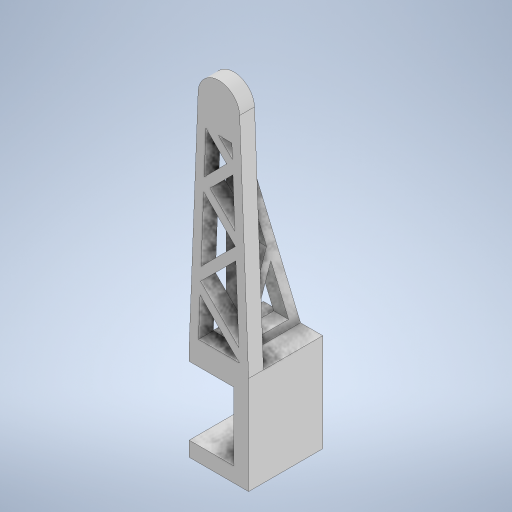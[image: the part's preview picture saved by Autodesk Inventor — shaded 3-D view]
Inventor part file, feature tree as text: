
AUTODESK INVENTOR PART (.ipt)
format: ipt  version: 2023 (Build 270158000, 158)  size: 342,016 bytes
history: native  units: mm
features: extrude x4, sketch x4, other x2
ambient origin geometry x8: Origin, YZ Plane, XZ Plane, XY Plane, X Axis, Y Axis, Z Axis, Center Point
bodies: Body1 (feature_tree)
feature tree (10):
  other  "솔리드1"
  extrude  "돌출1"  Depth=66.0mm
  extrude  "돌출2"  Depth=10.0mm
  other  "작업 평면1"
  extrude  "돌출3"  Depth=10.0mm
  extrude  "돌출4"  Depth=30.0mm
  sketch  "스케치1"
  sketch  "스케치2"
  sketch  "스케치3"
  sketch  "스케치4"
